# Revit family: MC-Miscellaneous Channel
name_source: partatom
category: Structural Framing
revit_build: Autodesk Revit Architecture 2012 (Build: 20110210_1515)
units: mm (PartAtom-declared; Revit-internal decimal feet)

## types (39) — shared parameters
Assembly Code = B10

## per-type parameters (varying)
| type | A | W | bf | d | tf | tw | x |
| MC18X58 | 17.1 in² | 58 | 0' - 4 3/16" | 1' - 6" | 0' - 0 5/8" | 0' - 0 11/16" | 0' - 0 7/8" |
| MC18X51.9 | 15.3 in² | 51.9 | 0' - 4 1/8" | 1' - 6" | 0' - 0 5/8" | 0' - 0 5/8" | 0' - 0 7/8" |
| MC18X45.8 | 13.5 in² | 45.8 | 0' - 4" | 1' - 6" | 0' - 0 5/8" | 0' - 0 1/2" | 0' - 0 7/8" |
| MC18X42.7 | 12.6 in² | 42.7 | 0' - 3 15/16" | 1' - 6" | 0' - 0 5/8" | 0' - 0 7/16" | 0' - 0 7/8" |
| MC13X50 | 14.7 in² | 50 | 0' - 4 7/16" | 1' - 1" | 0' - 0 5/8" | 0' - 0 13/16" | 0' - 1" |
| MC13X40 | 11.8 in² | 40 | 0' - 4 3/16" | 1' - 1" | 0' - 0 5/8" | 0' - 0 9/16" | 0' - 0 15/16" |
| MC13X35 | 10.3 in² | 35 | 0' - 4 1/16" | 1' - 1" | 0' - 0 5/8" | 0' - 0 7/16" | 0' - 1" |
| MC13X31.8 | 9.35 in² | 31.8 | 0' - 4" | 1' - 1" | 0' - 0 5/8" | 0' - 0 3/8" | 0' - 1" |
| MC12X50 | 14.7 in² | 50 | 0' - 4 1/8" | 1' - 0" | 0' - 0 11/16" | 0' - 0 13/16" | 0' - 1 1/16" |
| MC12X45 | 13.2 in² | 45 | 0' - 4" | 1' - 0" | 0' - 0 11/16" | 0' - 0 11/16" | 0' - 1 1/16" |
| MC12X40 | 11.8 in² | 40 | 0' - 3 7/8" | 1' - 0" | 0' - 0 11/16" | 0' - 0 9/16" | 0' - 1 1/16" |
| MC12X35 | 10.3 in² | 35 | 0' - 3 3/4" | 1' - 0" | 0' - 0 11/16" | 0' - 0 7/16" | 0' - 1 1/16" |
| MC12X31 | 9.12 in² | 31 | 0' - 3 11/16" | 1' - 0" | 0' - 0 11/16" | 0' - 0 3/8" | 0' - 1 1/16" |
| MC12X10.6 | 3.1 in² | 10.6 | 0' - 1 1/2" | 1' - 0" | 0' - 0 5/16" | 0' - 0 3/16" | 0' - 0 1/4" |
| MC10X41.1 | 12.1 in² | 41.1 | 0' - 4 5/16" | 0' - 10" | 0' - 0 9/16" | 0' - 0 13/16" | 0' - 1 1/16" |
| MC10X33.6 | 9.87 in² | 33.6 | 0' - 4 1/8" | 0' - 10" | 0' - 0 9/16" | 0' - 0 9/16" | 0' - 1 1/16" |
| MC10X28.5 | 8.37 in² | 28.5 | 0' - 3 15/16" | 0' - 10" | 0' - 0 9/16" | 0' - 0 7/16" | 0' - 1 1/8" |
| MC10X25 | 7.35 in² | 25 | 0' - 3 7/16" | 0' - 10" | 0' - 0 9/16" | 0' - 0 3/8" | 0' - 0 15/16" |
| MC10X22 | 6.45 in² | 22 | 0' - 3 5/16" | 0' - 10" | 0' - 0 9/16" | 0' - 0 5/16" | 0' - 1" |
| MC10X8.4 | 2.46 in² | 8.4 | 0' - 1 1/2" | 0' - 10" | 0' - 0 1/4" | 0' - 0 3/16" | 0' - 0 5/16" |
| MC10X6.5 | 1.95 in² | 6.5 | 0' - 1 3/16" | 0' - 10" | 0' - 0 3/16" | 0' - 0 1/8" | 0' - 0 3/16" |
| MC9X25.4 | 7.47 in² | 25.4 | 0' - 3 1/2" | 0' - 9" | 0' - 0 9/16" | 0' - 0 7/16" | 0' - 1" |
| MC9X23.9 | 7.02 in² | 23.9 | 0' - 3 7/16" | 0' - 9" | 0' - 0 9/16" | 0' - 0 3/8" | 0' - 1" |
| MC8X22.8 | 6.7 in² | 22.8 | 0' - 3 1/2" | 0' - 8" | 0' - 0 1/2" | 0' - 0 7/16" | 0' - 1" |
| MC8X21.4 | 6.28 in² | 21.4 | 0' - 3 7/16" | 0' - 8" | 0' - 0 1/2" | 0' - 0 3/8" | 0' - 1" |
| MC8X20 | 5.88 in² | 20 | 0' - 3" | 0' - 8" | 0' - 0 1/2" | 0' - 0 3/8" | 0' - 0 13/16" |
| MC8X18.7 | 5.5 in² | 18.7 | 0' - 3" | 0' - 8" | 0' - 0 1/2" | 0' - 0 3/8" | 0' - 0 7/8" |
| MC8X8.5 | 2.5 in² | 8.5 | 0' - 1 7/8" | 0' - 8" | 0' - 0 5/16" | 0' - 0 3/16" | 0' - 0 7/16" |
| MC7X22.7 | 6.67 in² | 22.7 | 0' - 3 5/8" | 0' - 7" | 0' - 0 1/2" | 0' - 0 1/2" | 0' - 1 1/16" |
| MC7X19.1 | 5.61 in² | 19.1 | 0' - 3 7/16" | 0' - 7" | 0' - 0 1/2" | 0' - 0 3/8" | 0' - 1 1/16" |
| MC6X18 | 5.29 in² | 18 | 0' - 3 1/2" | 0' - 6" | 0' - 0 1/2" | 0' - 0 3/8" | 0' - 1 1/8" |
| MC6X15.3 | 4.49 in² | 15.3 | 0' - 3 1/2" | 0' - 6" | 0' - 0 3/8" | 0' - 0 5/16" | 0' - 1 1/16" |
| MC6X16.3 | 4.79 in² | 16.3 | 0' - 3" | 0' - 6" | 0' - 0 1/2" | 0' - 0 3/8" | 0' - 0 15/16" |
| MC6X15.1 | 4.44 in² | 15.1 | 0' - 2 15/16" | 0' - 6" | 0' - 0 1/2" | 0' - 0 5/16" | 0' - 0 15/16" |
| MC6X12 | 3.53 in² | 12 | 0' - 2 1/2" | 0' - 6" | 0' - 0 3/8" | 0' - 0 5/16" | 0' - 0 11/16" |
| MC6x7 | 2.09 in² | 7 | 0' - 1 7/8" | 0' - 6" | 0' - 0 5/16" | 0' - 0 3/16" | 0' - 0 1/2" |
| MC6x6.5 | 1.95 in² | 6.5 | 0' - 1 7/8" | 0' - 6" | 0' - 0 5/16" | 0' - 0 1/8" | 0' - 0 1/2" |
| MC4x13.8 | 4.03 in² | 13.8 | 0' - 2 1/2" | 0' - 4" | 0' - 0 1/2" | 0' - 0 1/2" | 0' - 0 7/8" |
| MC3x7.1 | 2.11 in² | 7.1 | 0' - 1 15/16" | 0' - 3" | 0' - 0 3/8" | 0' - 0 5/16" | 0' - 0 5/8" |

## geometry (parser evidence)
native form markers: Sweep x1
no freeform markers — native parametric forms only
